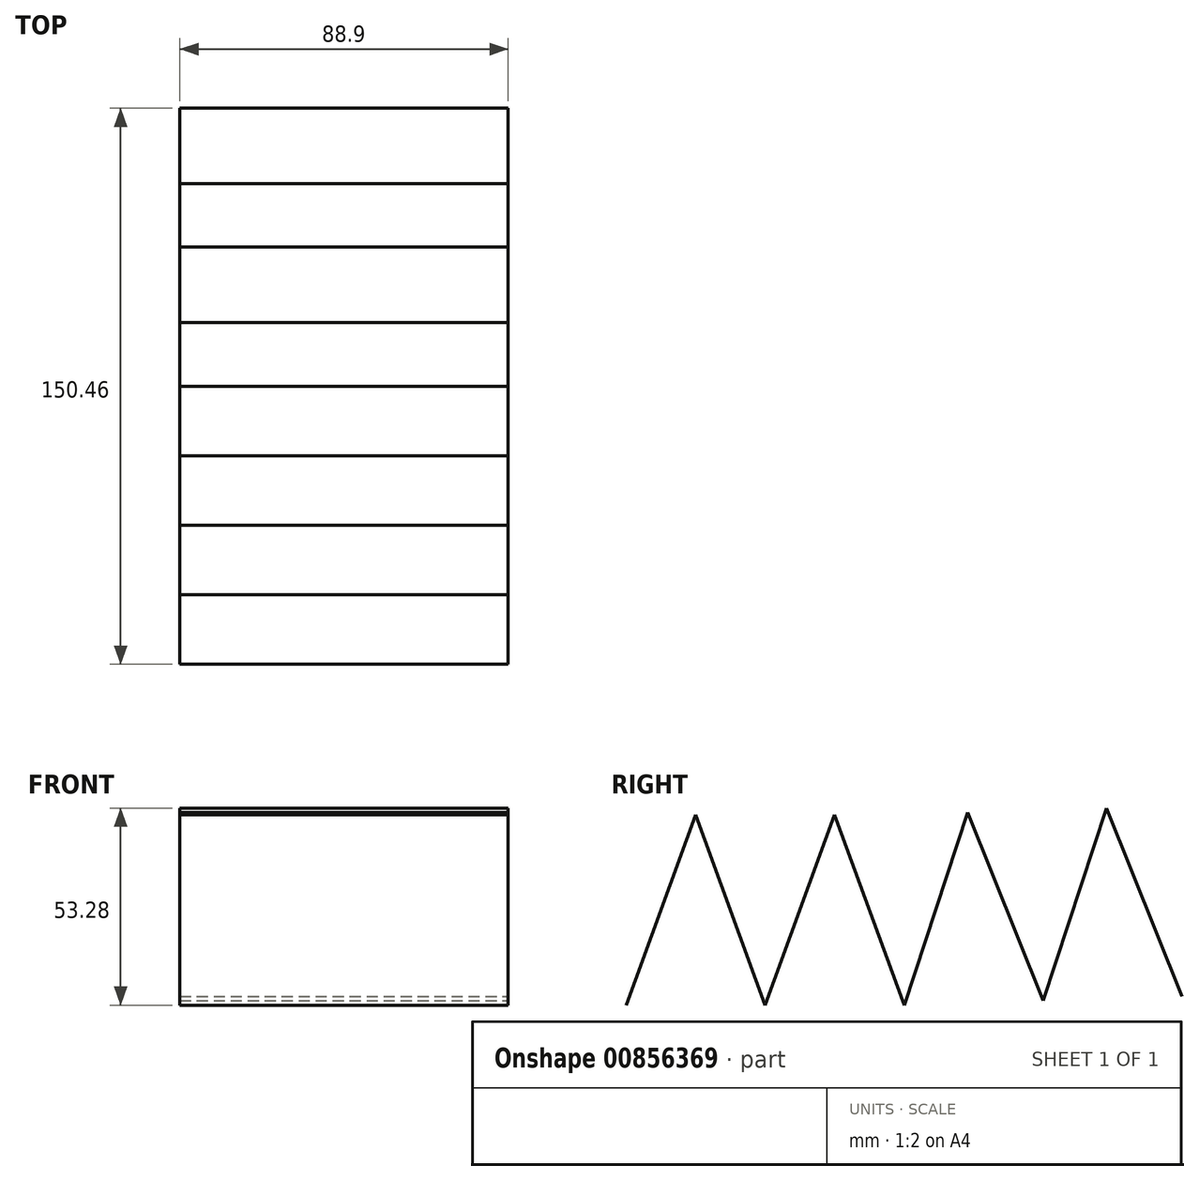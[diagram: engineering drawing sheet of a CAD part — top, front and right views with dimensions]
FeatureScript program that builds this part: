
annotation { "Feature Type Name" : "Feature", "Feature Type Description" : "" }
export const myFeature = defineFeature(function(context is Context, id is Id, definition is map)
    precondition{}
    {
        {
            var Q0;
            Q0=qCreatedBy(makeId("Right.planeOp"),FACE);
            var sketch = newSketch(context, id + "F0", { "sketchPlane" : qUnion([Q0])});
            skLineSegment(sketch, "E0", {"start": v(-87.62, 32.76) * mm, "end": v(-106.43, -18.78) * mm});
            skLineSegment(sketch, "E1", {"start": v(-87.62, 32.76) * mm, "end": v(-68.8, -18.78) * mm});
            skLineSegment(sketch, "E2", {"start": v(-50, 32.76) * mm, "end": v(-68.8, -18.78) * mm});
            skLineSegment(sketch, "E3", {"start": v(-50, 32.76) * mm, "end": v(-31.18, -18.78) * mm});
            skLineSegment(sketch, "E4.MirrorCS", {"start": v(23.61, 34.5) * mm, "end": v(44.03, -16.42) * mm});
            skLineSegment(sketch, "E5.MirrorCS", {"start": v(23.61, 34.5) * mm, "end": v(6.42, -17.6) * mm});
            skLineSegment(sketch, "E6.MirrorCS", {"start": v(-14, 33.33) * mm, "end": v(-31.18, -18.78) * mm});
            skLineSegment(sketch, "E7.MirrorCS", {"start": v(-14, 33.33) * mm, "end": v(6.42, -17.6) * mm});
            skSolve(sketch);
        }
        {
            var Q0;
            Q0=sQuery(id+"F0.wireOp",EDGE,"E7.MirrorCS");
            var Q1;
            Q1=sQuery(id+"F0.wireOp",EDGE,"E4.MirrorCS");
            var Q2;
            Q2=sQuery(id+"F0.wireOp",EDGE,"E5.MirrorCS");
            var Q3;
            Q3=sQuery(id+"F0.wireOp",EDGE,"E0");
            var Q4;
            Q4=sQuery(id+"F0.wireOp",EDGE,"E3");
            var Q5;
            Q5=sQuery(id+"F0.wireOp",EDGE,"E1");
            var Q6;
            Q6=sQuery(id+"F0.wireOp",EDGE,"E6.MirrorCS");
            var Q7;
            Q7=sQuery(id+"F0.wireOp",EDGE,"E2");
            extrude(context, id + "F1", {"bodyType" : ToolBodyType.SURFACE, "surfaceEntities" : qUnion([Q0, Q1, Q2, Q3, Q4, Q5, Q6, Q7]), "depth" : 88.9 * mm, "offsetDistance" : 25.4 * mm});
        }
    });
